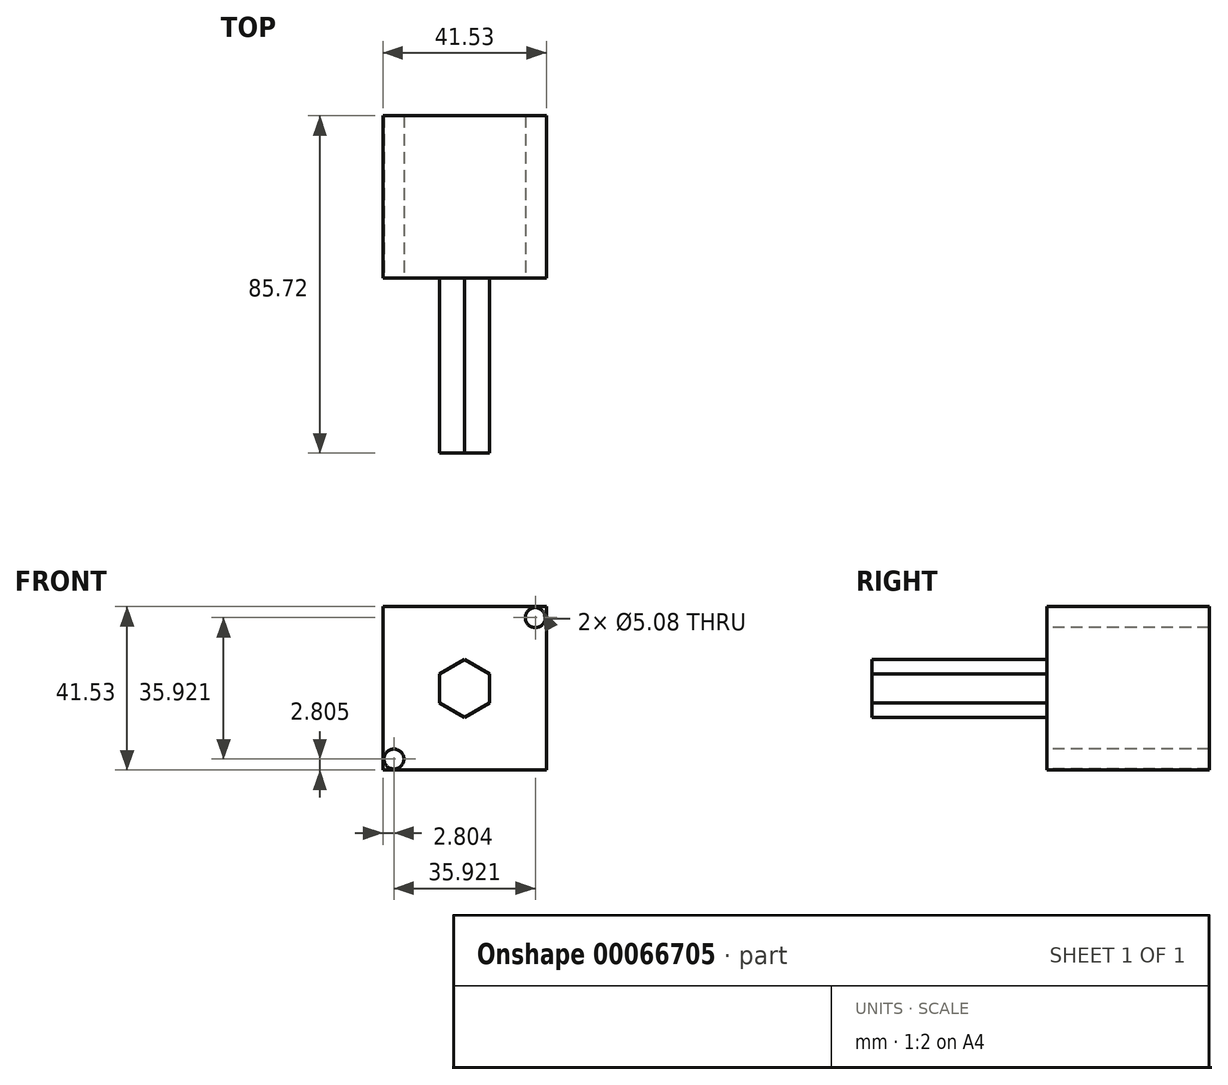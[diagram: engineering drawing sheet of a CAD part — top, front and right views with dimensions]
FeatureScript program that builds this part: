
annotation { "Feature Type Name" : "Feature", "Feature Type Description" : "" }
export const myFeature = defineFeature(function(context is Context, id is Id, definition is map)
    precondition{}
    {
        {
            var Q0;
            Q0=qCreatedBy(makeId("Front.planeOp"),FACE);
            var sketch = newSketch(context, id + "F0", { "sketchPlane" : qUnion([Q0])});
            skLineSegment(sketch, "E0.bottom", {"start": v(0, 0) * mm, "end": v(41.53, 0) * mm});
            skLineSegment(sketch, "E0.top", {"start": v(0, -41.53) * mm, "end": v(41.53, -41.53) * mm});
            skLineSegment(sketch, "E0.left", {"start": v(0, 0) * mm, "end": v(0, -41.53) * mm});
            skLineSegment(sketch, "E0.right", {"start": v(41.53, 0) * mm, "end": v(41.53, -41.53) * mm});
            skSolve(sketch);
        }
        {
            var Q0;
            Q0 = qSketchRegion(id + "F0", true);
            extrude(context, id + "F1", {"entities" : qUnion([Q0]), "depth" : 41.27 * mm});
        }
        {
            var Q0;
            Q0=makeQuery(id+"F1.opExtrude","CAP_FACE",FACE,{"disambiguationData":[OSD([sQuery(id+"F0.wireOp",EDGE,"E0.bottom"),sQuery(id+"F0.wireOp",EDGE,"E0.top"),sQuery(id+"F0.wireOp",EDGE,"E0.left"),sQuery(id+"F0.wireOp",EDGE,"E0.right")])],"isStart":false});
            var sketch = newSketch(context, id + "F2", { "sketchPlane" : qUnion([Q0])});
            skLineSegment(sketch, "E1", {"start": v(20.76, -20.76) * mm, "end": v(27.11, -20.76) * mm});
            skCircle(sketch, "E2.cCircle", {"center": v(20.76, -20.76) * mm, "radius": 6.35 * mm, "construction": true});
            skLineSegment(sketch, "E2.0", {"start": v(27.11, -17.1) * mm, "end": v(27.11, -24.43) * mm});
            skLineSegment(sketch, "E2.1", {"start": v(27.11, -24.43) * mm, "end": v(20.76, -28.1) * mm});
            skLineSegment(sketch, "E2.2", {"start": v(20.76, -28.1) * mm, "end": v(14.41, -24.43) * mm});
            skLineSegment(sketch, "E2.3", {"start": v(14.41, -24.43) * mm, "end": v(14.41, -17.1) * mm});
            skLineSegment(sketch, "E2.4", {"start": v(14.41, -17.1) * mm, "end": v(20.76, -13.43) * mm});
            skLineSegment(sketch, "E2.5", {"start": v(20.76, -13.43) * mm, "end": v(27.11, -17.1) * mm});
            skPoint(sketch, "E2.0.midPoint", {"position": v(27.11, -20.76) * mm});
            skLineSegment(sketch, "E3", {"start": v(20.76, 0) * mm, "end": v(20.76, -20.76) * mm});
            skLineSegment(sketch, "E4", {"start": v(20.76, -20.76) * mm, "end": v(0, -20.76) * mm});
            skSolve(sketch);
        }
        {
            var Q0;
            {var subQ0=sQuery(id+"F2.wireOp",EDGE,"E1");Q0=makeQuery(id+"F2.imprint","IMPRINT",FACE,{"disambiguationData":[TD([[makeQuery(id+"F2.imprint","IMPRINT",EDGE,{"derivedFrom":subQ0}),1.0]])]});}
            var Q1;
            {var subQ0=sQuery(id+"F2.wireOp",EDGE,"E1");Q1=makeQuery(id+"F2.imprint","IMPRINT",FACE,{"disambiguationData":[TD([[makeQuery(id+"F2.imprint","IMPRINT",EDGE,{"derivedFrom":subQ0}),-1.0]])]});}
            var Q2;
            {var subQ2=sQuery(id+"F2.wireOp",EDGE,"E2.2");Q2=makeQuery(id+"F2.imprint","IMPRINT",FACE,{"disambiguationData":[TD([[makeQuery(id+"F2.imprint","IMPRINT",EDGE,{"derivedFrom":subQ2}),-1.0]])]});}
            var Q3;
            {var subQ0=sQuery(id+"F2.wireOp",EDGE,"E2.4");Q3=makeQuery(id+"F2.imprint","IMPRINT",FACE,{"disambiguationData":[TD([[makeQuery(id+"F2.imprint","IMPRINT",EDGE,{"derivedFrom":subQ0}),-1.0]])]});}
            extrude(context, id + "F3", {"entities" : qUnion([Q0, Q1, Q2, Q3]), "depth" : 44.45 * mm});
        }
        {
            var Q0;
            Q0=makeQuery(id+"F1.opExtrude","CAP_FACE",FACE,{"disambiguationData":[OSD([sQuery(id+"F0.wireOp",EDGE,"E0.bottom"),sQuery(id+"F0.wireOp",EDGE,"E0.top"),sQuery(id+"F0.wireOp",EDGE,"E0.left"),sQuery(id+"F0.wireOp",EDGE,"E0.right")])],"isStart":false});
            var sketch = newSketch(context, id + "F4", { "sketchPlane" : qUnion([Q0])});
            skCircle(sketch, "E5", {"center": v(38.73, -2.8) * mm, "radius": 2.54 * mm});
            skCircle(sketch, "E6", {"center": v(2.8, -38.73) * mm, "radius": 2.54 * mm});
            skLineSegment(sketch, "E7", {"start": v(2.8, -38.73) * mm, "end": v(38.73, -2.8) * mm});
            skLineSegment(sketch, "E8", {"start": v(20.76, 0) * mm, "end": v(20.76, -20.76) * mm});
            skLineSegment(sketch, "E9", {"start": v(20.76, -20.76) * mm, "end": v(0, -20.76) * mm});
            skPoint(sketch, "E10", {"position": v(20.76, -20.76) * mm});
            skLineSegment(sketch, "E11", {"start": v(20.76, -20.76) * mm, "end": v(0, 0) * mm});
            skSolve(sketch);
        }
        {
            var Q0;
            Q0=makeQuery(id+"F4.imprint","IMPRINT",FACE,{"disambiguationData":[TD([[makeQuery(id+"F4.imprint","IMPRINT",EDGE,{"derivedFrom":sQuery(id+"F4.wireOp",EDGE,"E6")}),1.0]])]});
            var Q1;
            Q1=makeQuery(id+"F4.imprint","IMPRINT",FACE,{"disambiguationData":[TD([[makeQuery(id+"F4.imprint","IMPRINT",EDGE,{"derivedFrom":sQuery(id+"F4.wireOp",EDGE,"E5")}),1.0]])]});
            extrude(context, id + "F5", {"entities" : qUnion([Q0, Q1]), "operationType" : NewBodyOperationType.REMOVE, "oppositeDirection" : true, "depth" : 127 * mm});
        }
    });
